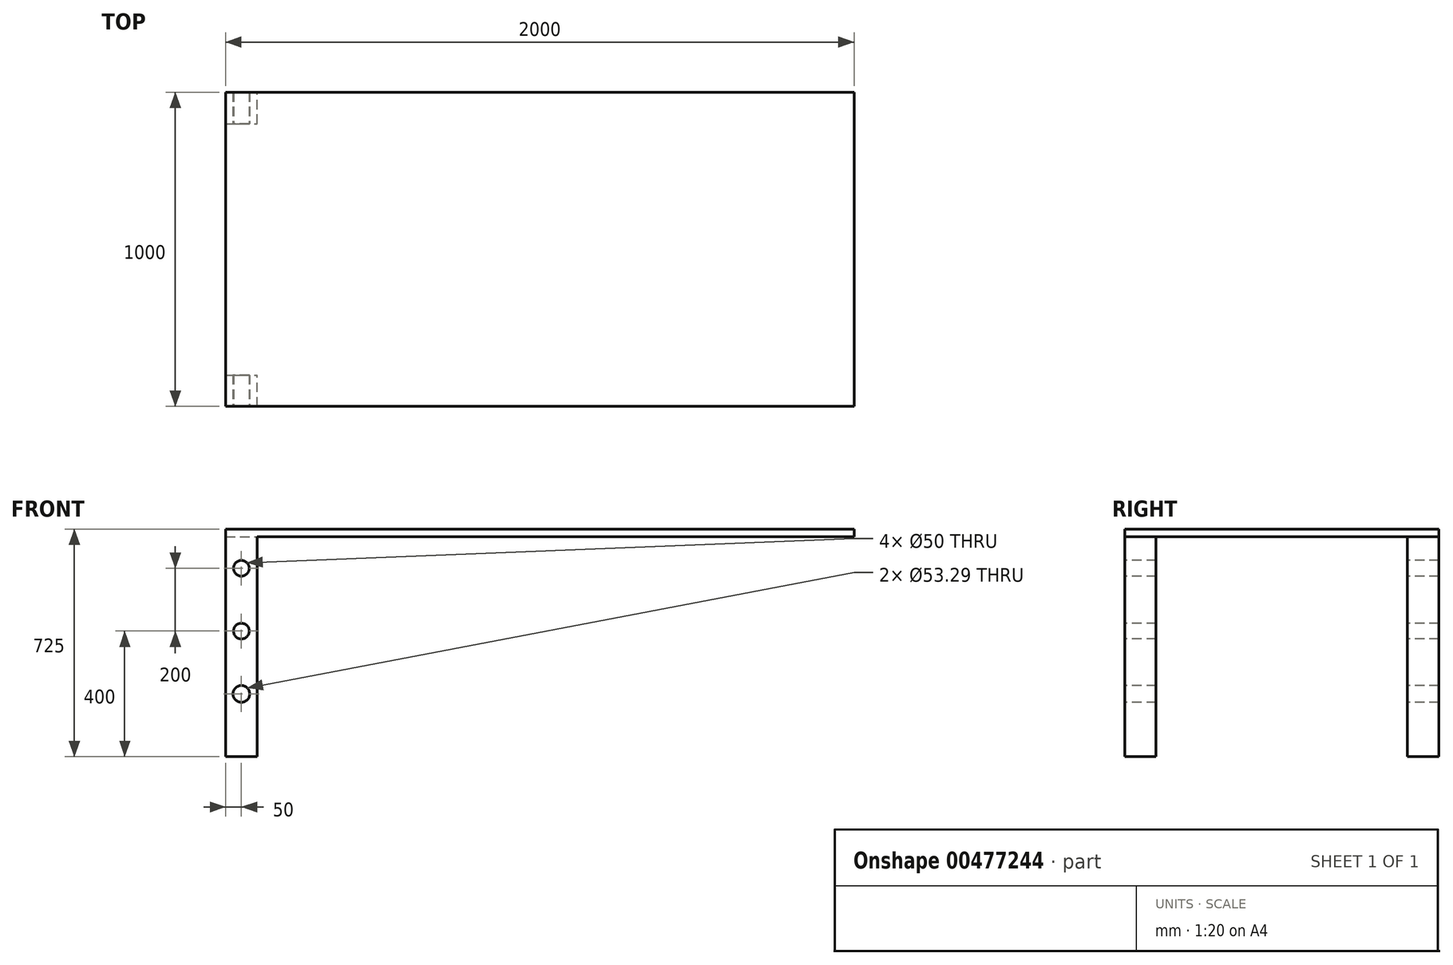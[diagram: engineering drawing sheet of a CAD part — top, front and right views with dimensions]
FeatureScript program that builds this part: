
annotation { "Feature Type Name" : "Feature", "Feature Type Description" : "" }
export const myFeature = defineFeature(function(context is Context, id is Id, definition is map)
    precondition{}
    {
        {
            var Q0;
            Q0=qCreatedBy(makeId("Top.planeOp"),FACE);
            var sketch = newSketch(context, id + "F0", { "sketchPlane" : qUnion([Q0])});
            skLineSegment(sketch, "E0.bottom", {"start": v(1000, 500) * mm, "end": v(-1000, 500) * mm});
            skLineSegment(sketch, "E0.top", {"start": v(1000, -500) * mm, "end": v(-1000, -500) * mm});
            skLineSegment(sketch, "E0.left", {"start": v(1000, 500) * mm, "end": v(1000, -500) * mm});
            skLineSegment(sketch, "E0.right", {"start": v(-1000, 500) * mm, "end": v(-1000, -500) * mm});
            skSolve(sketch);
        }
        {
            var Q0;
            Q0 = qSketchRegion(id + "F0", true);
            extrude(context, id + "F1", {"entities" : qUnion([Q0]), "flatOperationType" : FlatOperationType.REMOVE, "offsetDistance" : 25 * mm, "depth" : 25 * mm, "domain" : OperationDomain.MODEL});
        }
        {
            var Q0;
            Q0=makeQuery(id+"F1.opExtrude","CAP_FACE",FACE,{"disambiguationData":[OSD([sQuery(id+"F0.wireOp",EDGE,"E0.bottom"),sQuery(id+"F0.wireOp",EDGE,"E0.top"),sQuery(id+"F0.wireOp",EDGE,"E0.left"),sQuery(id+"F0.wireOp",EDGE,"E0.right")])],"isStart":true});
            var sketch = newSketch(context, id + "F2", { "sketchPlane" : qUnion([Q0])});
            skLineSegment(sketch, "E1.bottom", {"start": v(-1000, 500) * mm, "end": v(-900, 500) * mm});
            skLineSegment(sketch, "E1.top", {"start": v(-1000, 400) * mm, "end": v(-900, 400) * mm});
            skLineSegment(sketch, "E1.left", {"start": v(-1000, 500) * mm, "end": v(-1000, 400) * mm});
            skLineSegment(sketch, "E1.right", {"start": v(-900, 500) * mm, "end": v(-900, 400) * mm});
            skLineSegment(sketch, "E2.bottom", {"start": v(-1000, -400) * mm, "end": v(-900, -400) * mm});
            skLineSegment(sketch, "E2.top", {"start": v(-1000, -500) * mm, "end": v(-900, -500) * mm});
            skLineSegment(sketch, "E2.left", {"start": v(-1000, -400) * mm, "end": v(-1000, -500) * mm});
            skLineSegment(sketch, "E2.right", {"start": v(-900, -400) * mm, "end": v(-900, -500) * mm});
            skSolve(sketch);
        }
        {
            var Q0;
            {var subQ0=sQuery(id+"F2.wireOp",EDGE,"E1.bottom");Q0=makeQuery(id+"FMo4bRB5P6w2gM2_1.1.F4.boolean.opBoolean","MERGE",FACE,{"derivedFrom":[makeQuery(id+"F4.boolean.opBoolean","MERGE",FACE,{"derivedFrom":[makeQuery(id+"F1.opExtrude","SWEPT_FACE",FACE,{"disambiguationData":[OSD([sQuery(id+"F0.wireOp",EDGE,"E0.top")])]}),makeQuery(id+"F4.opExtrude","SWEPT_FACE",FACE,{"disambiguationData":[OSD([subQ0])]})]}),makeQuery(id+"FMo4bRB5P6w2gM2_1.1.F4.opExtrude","SWEPT_FACE",FACE,{"disambiguationData":[OSD([subQ0])]})]});}
            var sketch = newSketch(context, id + "F3", { "sketchPlane" : qUnion([Q0])});
            skCircle(sketch, "E3", {"center": v(-950, -100) * mm, "radius": 25 * mm});
            skCircle(sketch, "E4", {"center": v(-950, -300) * mm, "radius": 25 * mm});
            skCircle(sketch, "E5", {"center": v(-950, -500) * mm, "radius": 26.64 * mm});
            skSolve(sketch);
        }
        {
            var Q0;
            Q0 = qSketchRegion(id + "F2", true);
            extrude(context, id + "F4", {"entities" : qUnion([Q0]), "operationType" : NewBodyOperationType.ADD, "flatOperationType" : FlatOperationType.REMOVE, "offsetDistance" : 25 * mm, "depth" : 700 * mm, "domain" : OperationDomain.MODEL});
        }
        {
            var Q0;
            Q0 = qSketchRegion(id + "F3", true);
            extrude(context, id + "F5", {"entities" : qUnion([Q0]), "operationType" : NewBodyOperationType.REMOVE, "endBound" : BoundingType.THROUGH_ALL, "oppositeDirection" : true, "depth" : 25 * mm});
        }
        {
            var Q0;
            {var subQ0=sQuery(id+"F2.wireOp",EDGE,"E1.bottom");Q0=makeQuery(id+"FMo4bRB5P6w2gM2_1.1.F4.boolean.opBoolean","MERGE",FACE,{"derivedFrom":[makeQuery(id+"F4.boolean.opBoolean","MERGE",FACE,{"derivedFrom":[makeQuery(id+"F1.opExtrude","SWEPT_FACE",FACE,{"disambiguationData":[OSD([sQuery(id+"F0.wireOp",EDGE,"E0.top")])]}),makeQuery(id+"F4.opExtrude","SWEPT_FACE",FACE,{"disambiguationData":[OSD([subQ0])]})]}),makeQuery(id+"FMo4bRB5P6w2gM2_1.1.F4.opExtrude","SWEPT_FACE",FACE,{"disambiguationData":[OSD([subQ0])]})]});}
            var sketch = newSketch(context, id + "F6", { "sketchPlane" : qUnion([Q0])});
            skCircle(sketch, "E6", {"center": v(508.73, -680.18) * mm, "radius": 138.46 * mm});
            skSolve(sketch);
        }
        {
            var Q0;
            Q0=makeQuery(id+"F4.opExtrude","SWEPT_FACE",FACE,{"disambiguationData":[OSD([sQuery(id+"F2.wireOp",EDGE,"E2.right")])]});
            var sketch = newSketch(context, id + "F7", { "sketchPlane" : qUnion([Q0])});
            skLineSegment(sketch, "E7.bottom", {"start": v(779.6, -394.17) * mm, "end": v(661.06, -394.17) * mm});
            skLineSegment(sketch, "E7.top", {"start": v(779.6, -236.63) * mm, "end": v(661.06, -236.63) * mm});
            skLineSegment(sketch, "E7.left", {"start": v(779.6, -394.17) * mm, "end": v(779.6, -236.63) * mm});
            skLineSegment(sketch, "E7.right", {"start": v(661.06, -394.17) * mm, "end": v(661.06, -236.63) * mm});
            skSolve(sketch);
        }
        {
            var Q0;
            Q0=makeQuery(id+"F6.imprint","IMPRINT",FACE,{"disambiguationData":[TD([[makeQuery(id+"F6.imprint","IMPRINT",EDGE,{"derivedFrom":sQuery(id+"F6.wireOp",EDGE,"E6")}),1.0]])]});
            var Q1;
            Q1=makeQuery(id+"F7.imprint","IMPRINT",FACE,{"disambiguationData":[TD([[makeQuery(id+"F7.imprint","IMPRINT",EDGE,{"derivedFrom":sQuery(id+"F7.wireOp",EDGE,"E7.bottom")}),-1.0]])]});
            loft(context, id + "F8", {"sheetProfilesArray" : [{ "sheetProfileEntities" : qUnion([Q0]) }, { "sheetProfileEntities" : qUnion([Q1]) }]});
        }
        {
            var Q0;
            {var subQ0=sQuery(id+"F7.wireOp",EDGE,"E7.bottom");var subQ1=sQuery(id+"F7.wireOp",EDGE,"E7.left");var subQ2=sQuery(id+"F7.wireOp",EDGE,"E7.top");var subQ3=sQuery(id+"F7.wireOp",EDGE,"E7.right");var subQ4=sQuery(id+"F6.wireOp",EDGE,"E6");Q0=makeQuery(id+"F8.opLoft","SWEPT_FACE",FACE,{"disambiguationData":[OSD([subQ4,subQ0,subQ2,subQ1,subQ3]),TDD([makeQuery(id+"F6.imprint","IMPRINT",EDGE,{"derivedFrom":subQ4}),makeQuery(id+"F7.imprint","INTERSECT",VERTEX,{"derivedFrom":[subQ0,subQ1]}),makeQuery(id+"F7.imprint","INTERSECT",VERTEX,{"derivedFrom":[subQ0,subQ3]}),makeQuery(id+"F7.imprint","INTERSECT",VERTEX,{"derivedFrom":[subQ2,subQ1]}),makeQuery(id+"F7.imprint","IMPRINT",EDGE,{"derivedFrom":subQ0})])]});}
            shell(context, id + "F9", {"entities" : qUnion([Q0]), "thickness" : 2.5 * mm});
        }
        {
            var Q0;
            Q0=makeQuery(id+"F8.opLoft","SWEPT_BODY",BODY,{"disambiguationData":[OSD([makeQuery(id+"F6.imprint","IMPRINT",FACE,{"disambiguationData":[TD([[makeQuery(id+"F6.imprint","IMPRINT",EDGE,{"derivedFrom":sQuery(id+"F6.wireOp",EDGE,"E6")}),1.0]])]}),makeQuery(id+"F7.imprint","IMPRINT",FACE,{"disambiguationData":[TD([[makeQuery(id+"F7.imprint","IMPRINT",EDGE,{"derivedFrom":sQuery(id+"F7.wireOp",EDGE,"E7.bottom")}),-1.0]])]})])]});
            deleteBodies(context, id + "F10", {"entities" : qUnion([Q0])});
        }
    });
